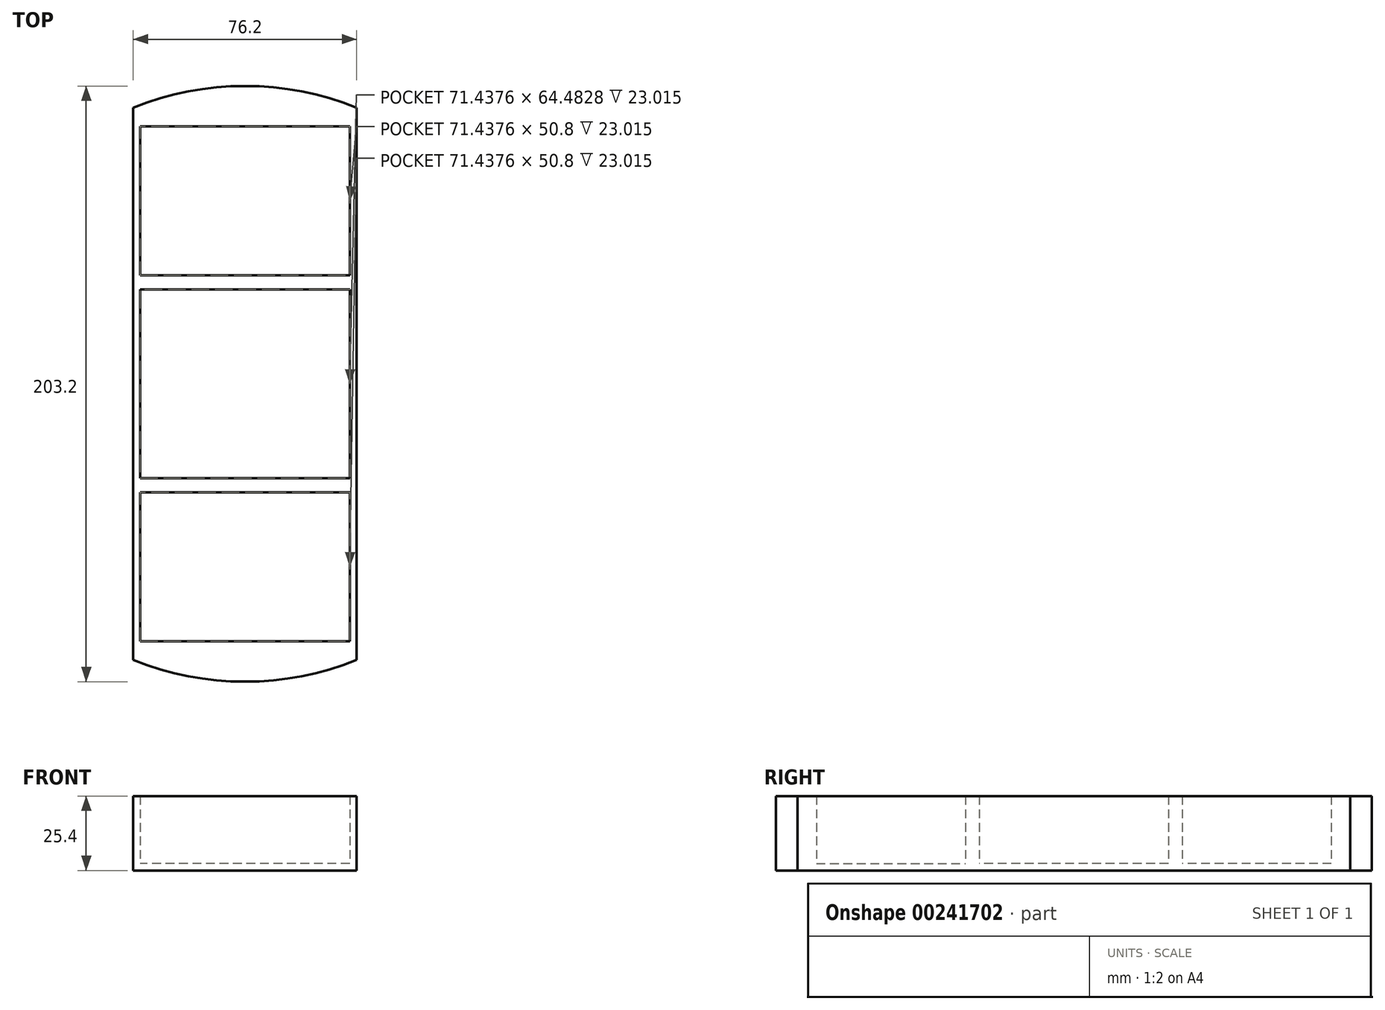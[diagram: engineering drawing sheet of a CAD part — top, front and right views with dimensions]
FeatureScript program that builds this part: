
annotation { "Feature Type Name" : "Feature", "Feature Type Description" : "" }
export const myFeature = defineFeature(function(context is Context, id is Id, definition is map)
    precondition{}
    {
        {
            var Q0;
            Q0=qCreatedBy(makeId("Top.planeOp"),FACE);
            var sketch = newSketch(context, id + "F0", { "sketchPlane" : qUnion([Q0])});
            skPoint(sketch, "E0.middle", {"position": v(0, 0) * mm});
            skArc(sketch, "E1", {"start": v(-38.1, -94.19) * mm, "mid": v(-19.4, -99.73) * mm, "end": v(0, -101.6) * mm});
            skArc(sketch, "E2", {"start": v(0, -101.6) * mm, "mid": v(19.4, -99.73) * mm, "end": v(38.1, -94.19) * mm});
            skArc(sketch, "E3", {"start": v(0, 101.6) * mm, "mid": v(-19.4, 99.73) * mm, "end": v(-38.1, 94.19) * mm});
            skArc(sketch, "E4", {"start": v(38.1, 94.19) * mm, "mid": v(19.4, 99.73) * mm, "end": v(0, 101.6) * mm});
            skLineSegment(sketch, "E5", {"start": v(-38.1, -94.19) * mm, "end": v(-38.1, 94.19) * mm});
            skLineSegment(sketch, "E6", {"start": v(38.1, 94.19) * mm, "end": v(38.1, -94.19) * mm});
            skSolve(sketch);
        }
        {
            var Q0;
            Q0=makeQuery(id+"F0.imprint","IMPRINT",FACE,{"disambiguationData":[TD([[makeQuery(id+"F0.imprint","IMPRINT",EDGE,{"derivedFrom":sQuery(id+"F0.wireOp",EDGE,"E1")}),1.0]])]});
            extrude(context, id + "F1", {"entities" : qUnion([Q0]), "depth" : 25.4 * mm});
        }
        {
            var Q0;
            Q0=makeQuery(id+"F1.opExtrude","CAP_FACE",FACE,{"disambiguationData":[OSD([sQuery(id+"F0.wireOp",EDGE,"E1"),sQuery(id+"F0.wireOp",EDGE,"E2"),sQuery(id+"F0.wireOp",EDGE,"E3"),sQuery(id+"F0.wireOp",EDGE,"E4"),sQuery(id+"F0.wireOp",EDGE,"E5"),sQuery(id+"F0.wireOp",EDGE,"E6")])],"isStart":false});
            shell(context, id + "F2", {"entities" : qUnion([Q0]), "thickness" : 2.38 * mm});
        }
        {
            var Q0;
            Q0=makeQuery(id+"F2.opShell","OFFSET_FACE",FACE,{"disambiguationData":[OSD([sQuery(id+"F0.wireOp",EDGE,"E1"),sQuery(id+"F0.wireOp",EDGE,"E2"),sQuery(id+"F0.wireOp",EDGE,"E3"),sQuery(id+"F0.wireOp",EDGE,"E4"),sQuery(id+"F0.wireOp",EDGE,"E5"),sQuery(id+"F0.wireOp",EDGE,"E6")])]});
            var sketch = newSketch(context, id + "F3", { "sketchPlane" : qUnion([Q0])});
            skLineSegment(sketch, "E7.bottom", {"start": v(-35.72, -92.57) * mm, "end": v(35.72, -92.57) * mm});
            skLineSegment(sketch, "E7.top", {"start": v(-35.72, 92.57) * mm, "end": v(35.72, 92.57) * mm});
            skLineSegment(sketch, "E7.left", {"start": v(-35.72, -92.57) * mm, "end": v(-35.72, 92.57) * mm});
            skLineSegment(sketch, "E7.right", {"start": v(35.72, -92.57) * mm, "end": v(35.72, 92.57) * mm});
            skLineSegment(sketch, "E8", {"start": v(35.72, 92.57) * mm, "end": v(35.72, 87.8) * mm});
            skPoint(sketch, "E9.endSnap0", {"position": v(0, 92.57) * mm});
            skPoint(sketch, "E10.endSnap0", {"position": v(0, -92.57) * mm});
            skLineSegment(sketch, "E11", {"start": v(-35.72, -37) * mm, "end": v(35.72, -37) * mm});
            skLineSegment(sketch, "E12", {"start": v(35.72, -32.24) * mm, "end": v(-35.72, -32.24) * mm});
            skLineSegment(sketch, "E13", {"start": v(35.72, 37) * mm, "end": v(-35.72, 37) * mm});
            skLineSegment(sketch, "E14", {"start": v(35.72, 32.24) * mm, "end": v(-35.72, 32.24) * mm});
            skLineSegment(sketch, "E15", {"start": v(-35.72, 87.8) * mm, "end": v(35.72, 87.8) * mm});
            skLineSegment(sketch, "E16", {"start": v(35.72, -87.8) * mm, "end": v(-35.72, -87.8) * mm});
            skSolve(sketch);
        }
        {
            var Q0;
            Q0=makeQuery(id+"F3.imprint","IMPRINT",FACE,{"disambiguationData":[TD([[makeQuery(id+"F3.imprint","IMPRINT",EDGE,{"derivedFrom":sQuery(id+"F3.wireOp",EDGE,"E7.bottom")}),1.0]])]});
            extrude(context, id + "F4", {"entities" : qUnion([Q0]), "operationType" : NewBodyOperationType.ADD, "depth" : 4.76 * mm});
        }
        {
            var Q0;
            {var subQ0=sQuery(id+"F3.wireOp",EDGE,"E7.bottom");Q0=makeQuery(id+"F3.imprint","IMPRINT",FACE,{"disambiguationData":[TD([[makeQuery(id+"F3.imprint","IMPRINT",EDGE,{"derivedFrom":subQ0}),1.0]])]});}
            var Q1;
            {var subQ0=sQuery(id+"F3.wireOp",EDGE,"E11");Q1=makeQuery(id+"F3.imprint","IMPRINT",FACE,{"disambiguationData":[TD([[makeQuery(id+"F3.imprint","IMPRINT",EDGE,{"derivedFrom":subQ0}),1.0]])]});}
            var Q2;
            {var subQ0=sQuery(id+"F3.wireOp",EDGE,"E13");Q2=makeQuery(id+"F3.imprint","IMPRINT",FACE,{"disambiguationData":[TD([[makeQuery(id+"F3.imprint","IMPRINT",EDGE,{"derivedFrom":subQ0}),1.0]])]});}
            var Q3;
            {var subQ0=sQuery(id+"F3.wireOp",EDGE,"E7.top");Q3=makeQuery(id+"F3.imprint","IMPRINT",FACE,{"disambiguationData":[TD([[makeQuery(id+"F3.imprint","IMPRINT",EDGE,{"derivedFrom":subQ0}),-1.0]])]});}
            extrude(context, id + "F5", {"entities" : qUnion([Q0, Q1, Q2, Q3]), "operationType" : NewBodyOperationType.ADD, "depth" : 23.01 * mm});
        }
        {
            var Q0;
            {var subQ0=sQuery(id+"F0.wireOp",EDGE,"E4");var subQ1=sQuery(id+"F0.wireOp",EDGE,"E3");var subQ3=sQuery(id+"F0.wireOp",EDGE,"E5");var subQ4=sQuery(id+"F0.wireOp",EDGE,"E6");Q0=makeQuery(id+"F5.boolean.opBoolean","SPLIT",FACE,{"disambiguationData":[TD([makeQuery(id+"F5.opExtrude","SWEPT_FACE",FACE,{"disambiguationData":[OSD([sQuery(id+"F3.wireOp",EDGE,"E7.top")])]})])],"derivedFrom":makeQuery(id+"F4.boolean.opBoolean","SPLIT",FACE,{"disambiguationData":[TD([makeQuery(id+"F2.opShell","OFFSET_FACE",FACE,{"disambiguationData":[OSD([subQ3])]})])],"derivedFrom":makeQuery(id+"F2.opShell","OFFSET_FACE",FACE,{"disambiguationData":[OSD([sQuery(id+"F0.wireOp",EDGE,"E1"),sQuery(id+"F0.wireOp",EDGE,"E2"),subQ1,subQ0,subQ3,subQ4])]})})});}
            extrude(context, id + "F6", {"entities" : qUnion([Q0]), "operationType" : NewBodyOperationType.ADD, "depth" : 23.01 * mm});
        }
        {
            var Q0;
            {var subQ0=sQuery(id+"F0.wireOp",EDGE,"E2");var subQ1=sQuery(id+"F0.wireOp",EDGE,"E1");Q0=makeQuery(id+"F4.boolean.opBoolean","SPLIT",FACE,{"disambiguationData":[TD([makeQuery(id+"F4.opExtrude","SWEPT_FACE",FACE,{"disambiguationData":[OSD([sQuery(id+"F3.wireOp",EDGE,"E7.bottom")])]})])],"derivedFrom":makeQuery(id+"F2.opShell","OFFSET_FACE",FACE,{"disambiguationData":[OSD([subQ1,subQ0,sQuery(id+"F0.wireOp",EDGE,"E3"),sQuery(id+"F0.wireOp",EDGE,"E4"),sQuery(id+"F0.wireOp",EDGE,"E5"),sQuery(id+"F0.wireOp",EDGE,"E6")])]})});}
            extrude(context, id + "F7", {"entities" : qUnion([Q0]), "operationType" : NewBodyOperationType.ADD, "depth" : 23.01 * mm});
        }
    });
